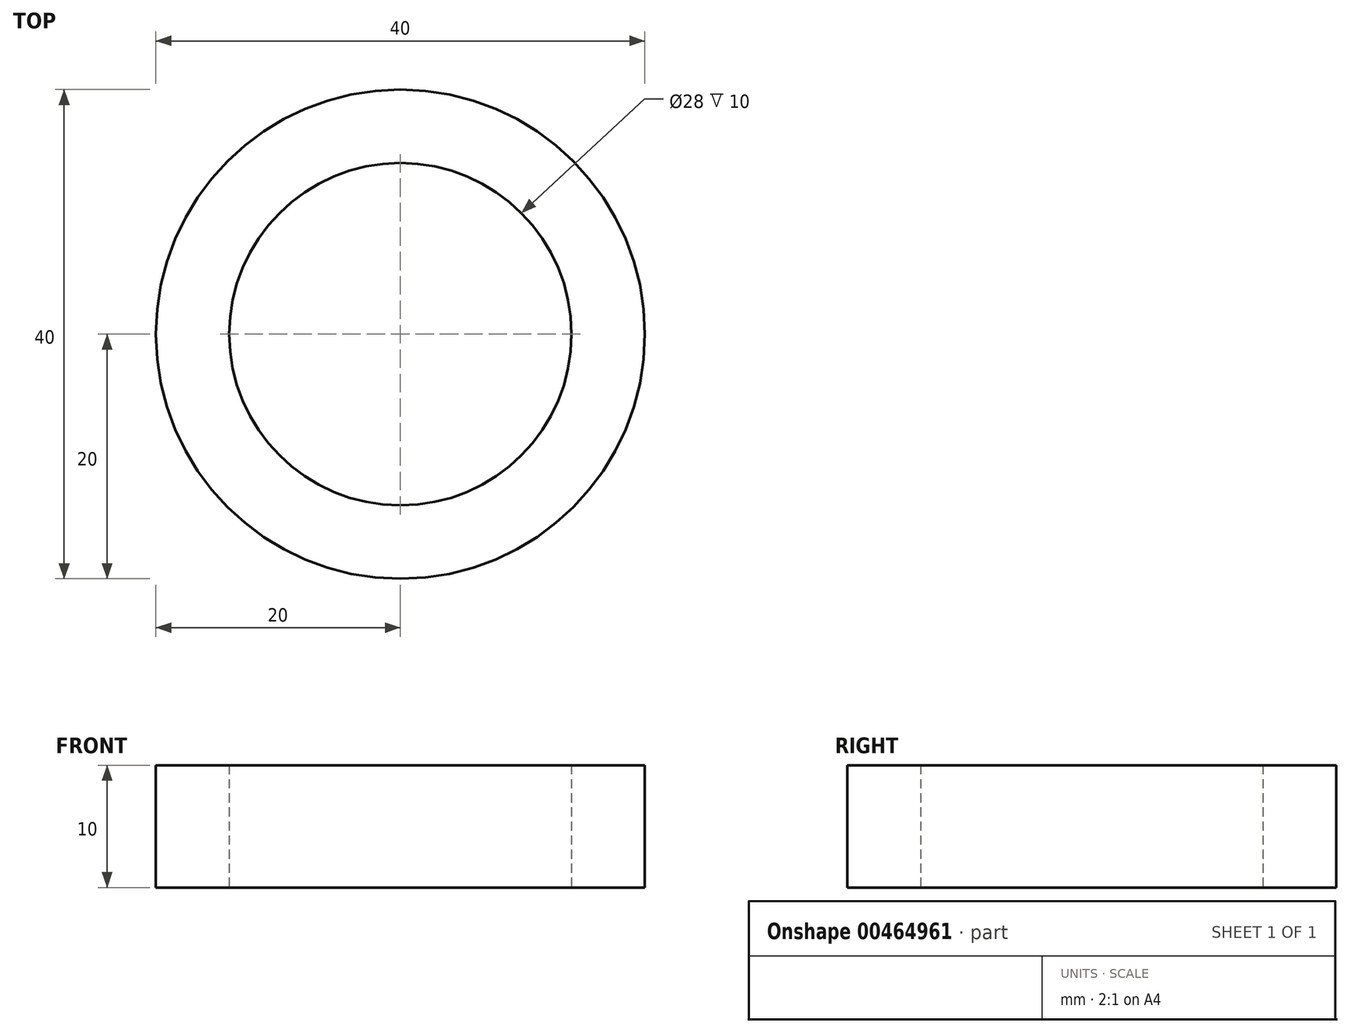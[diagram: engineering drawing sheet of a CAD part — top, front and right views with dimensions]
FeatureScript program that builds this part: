
annotation { "Feature Type Name" : "Feature", "Feature Type Description" : "" }
export const myFeature = defineFeature(function(context is Context, id is Id, definition is map)
    precondition{}
    {
        {
            var Q0;
            Q0=qCreatedBy(makeId("Top.planeOp"),FACE);
            var sketch = newSketch(context, id + "F0", { "sketchPlane" : qUnion([Q0])});
            skCircle(sketch, "E0", {"center": v(0, 0) * mm, "radius": 20 * mm});
            skCircle(sketch, "E1", {"center": v(0, 0) * mm, "radius": 14 * mm});
            skSolve(sketch);
        }
        {
            var Q0;
            Q0=makeQuery(id+"F0.imprint","IMPRINT",FACE,{"disambiguationData":[TD([[makeQuery(id+"F0.imprint","IMPRINT",EDGE,{"derivedFrom":sQuery(id+"F0.wireOp",EDGE,"E0")}),1.0]])]});
            extrude(context, id + "F1", {"entities" : qUnion([Q0]), "depth" : (10) * mm});
        }
    });
